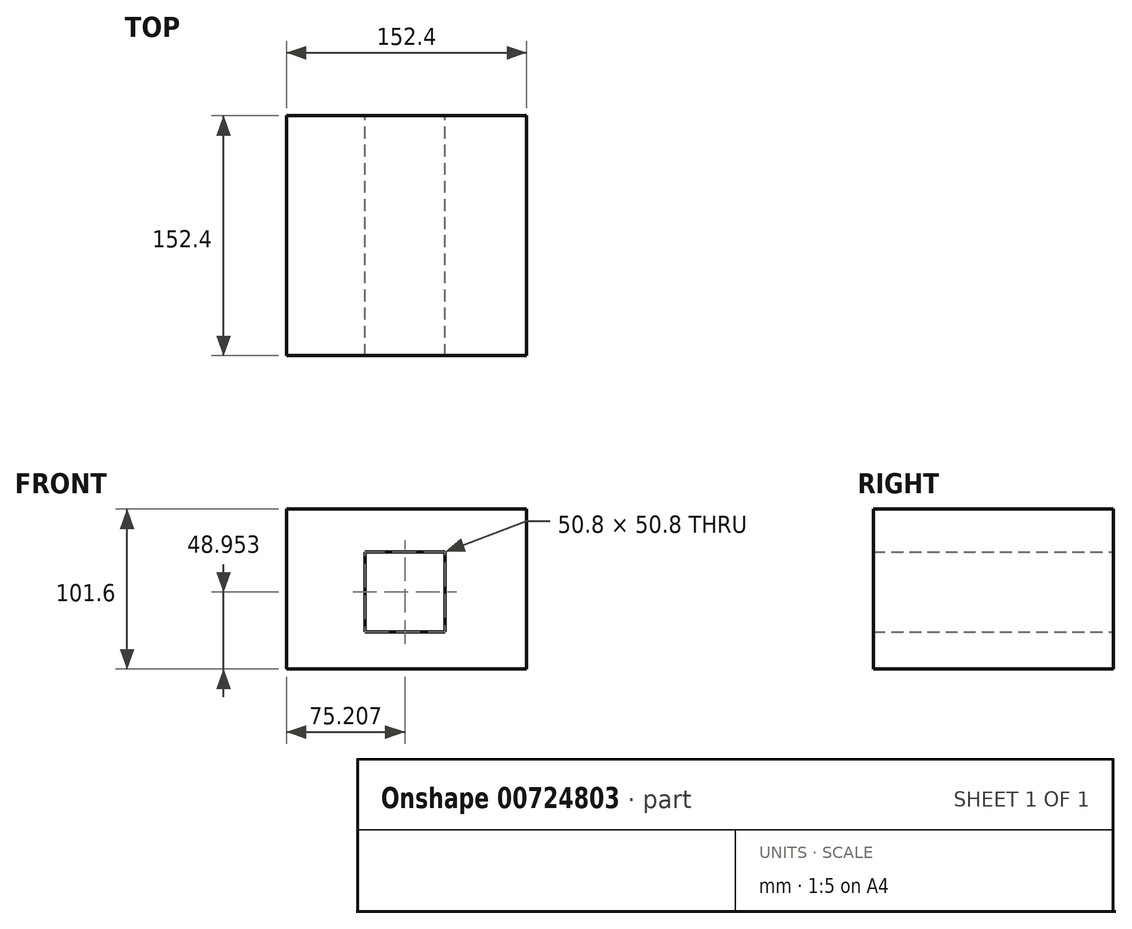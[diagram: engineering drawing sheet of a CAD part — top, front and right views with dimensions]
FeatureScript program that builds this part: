
annotation { "Feature Type Name" : "Feature", "Feature Type Description" : "" }
export const myFeature = defineFeature(function(context is Context, id is Id, definition is map)
    precondition{}
    {
        {
            var Q0;
            Q0=qCreatedBy(makeId("Front.planeOp"),FACE);
            var sketch = newSketch(context, id + "F0", { "sketchPlane" : qUnion([Q0])});
            skLineSegment(sketch, "E0", {"start": v(-74.02, -39.27) * mm, "end": v(78.38, -39.27) * mm});
            skLineSegment(sketch, "E1", {"start": v(78.38, -39.27) * mm, "end": v(78.38, 62.33) * mm});
            skLineSegment(sketch, "E2", {"start": v(78.38, 62.33) * mm, "end": v(-74.02, 62.33) * mm});
            skLineSegment(sketch, "E3", {"start": v(-74.02, 62.33) * mm, "end": v(-74.02, -39.27) * mm});
            skLineSegment(sketch, "E4.bottom", {"start": v(26.59, -15.72) * mm, "end": v(-24.21, -15.72) * mm});
            skLineSegment(sketch, "E4.top", {"start": v(26.59, 35.08) * mm, "end": v(-24.21, 35.08) * mm});
            skLineSegment(sketch, "E4.left", {"start": v(26.59, -15.72) * mm, "end": v(26.59, 35.08) * mm});
            skLineSegment(sketch, "E4.right", {"start": v(-24.21, -15.72) * mm, "end": v(-24.21, 35.08) * mm});
            skPoint(sketch, "E4.middle", {"position": v(1.19, 9.68) * mm});
            skSolve(sketch);
        }
        {
            var Q0;
            Q0 = qSketchRegion(id + "F0", true);
            extrude(context, id + "F1", {"entities" : qUnion([Q0]), "depth" : 152.4 * mm, "offsetDistance" : 25.4 * mm});
        }
    });
